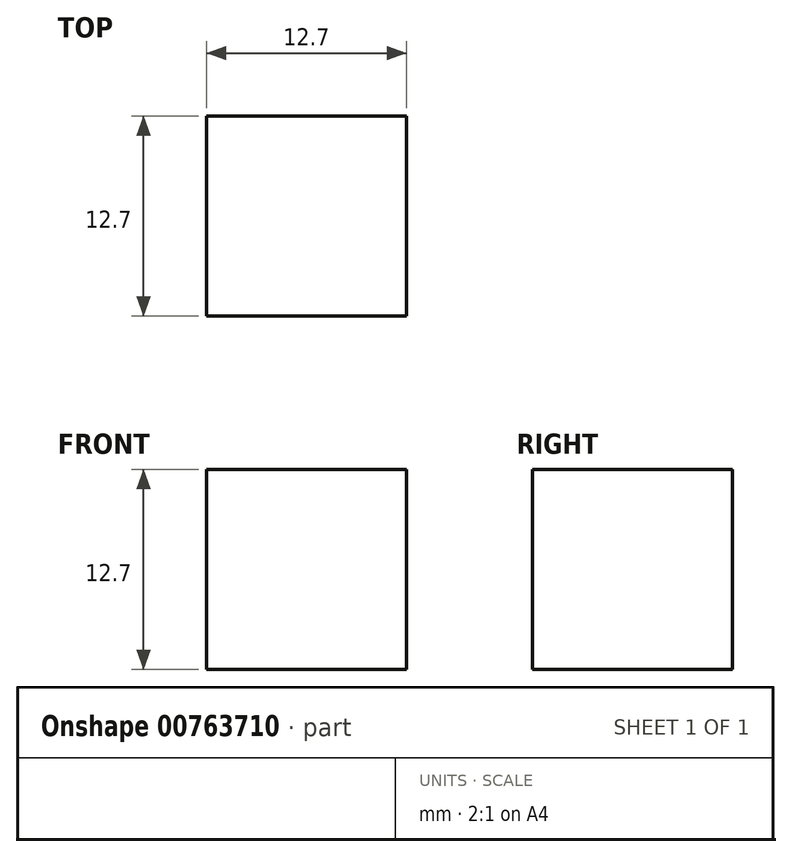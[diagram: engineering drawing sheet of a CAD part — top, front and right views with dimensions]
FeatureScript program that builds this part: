
annotation { "Feature Type Name" : "Feature", "Feature Type Description" : "" }
export const myFeature = defineFeature(function(context is Context, id is Id, definition is map)
    precondition{}
    {
        {
            var Q0;
            Q0=qCreatedBy(makeId("Top.planeOp"),FACE);
            var sketch = newSketch(context, id + "F0", { "sketchPlane" : qUnion([Q0])});
            skLineSegment(sketch, "E0.bottom", {"start": v(-60.64, 27.1) * mm, "end": v(-47.94, 27.1) * mm});
            skLineSegment(sketch, "E0.top", {"start": v(-60.64, 14.4) * mm, "end": v(-47.94, 14.4) * mm});
            skLineSegment(sketch, "E0.left", {"start": v(-60.64, 27.1) * mm, "end": v(-60.64, 14.4) * mm});
            skLineSegment(sketch, "E0.right", {"start": v(-47.94, 27.1) * mm, "end": v(-47.94, 14.4) * mm});
            skSolve(sketch);
        }
        {
            var Q0;
            Q0 = qSketchRegion(id + "F0", true);
            var Q1;
            Q1=makeQuery(id+"F0.imprint","IMPRINT",FACE,{"disambiguationData":[TD([[makeQuery(id+"F0.imprint","IMPRINT",EDGE,{"derivedFrom":sQuery(id+"F0.wireOp",EDGE,"E0.bottom")}),-1.0]])]});
            extrude(context, id + "F1", {"entities" : qUnion([Q0, Q1]), "depth" : 12.7 * mm, "offsetDistance" : 25.4 * mm});
        }
    });
